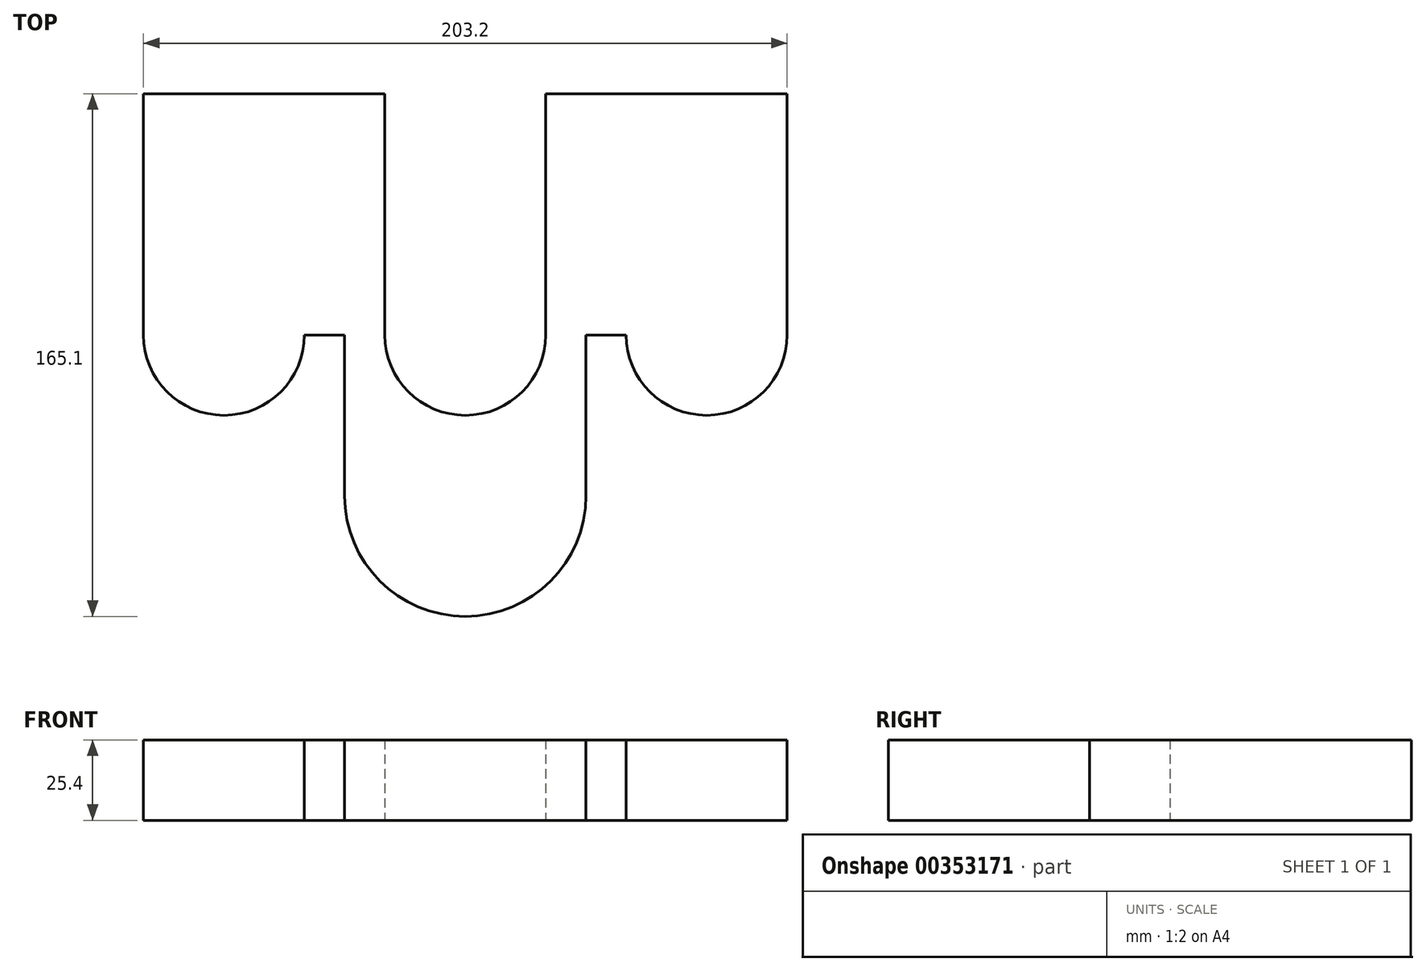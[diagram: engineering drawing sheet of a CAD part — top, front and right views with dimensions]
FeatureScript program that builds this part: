
annotation { "Feature Type Name" : "Feature", "Feature Type Description" : "" }
export const myFeature = defineFeature(function(context is Context, id is Id, definition is map)
    precondition{}
    {
        {
            var Q0;
            Q0=qCreatedBy(makeId("Top.planeOp"),FACE);
            var sketch = newSketch(context, id + "F0", { "sketchPlane" : qUnion([Q0])});
            skLineSegment(sketch, "E0", {"start": v(-50.8, 37.25) * mm, "end": v(25.4, 37.25) * mm});
            skLineSegment(sketch, "E1", {"start": v(25.4, 37.25) * mm, "end": v(25.4, -38.95) * mm});
            skLineSegment(sketch, "E2", {"start": v(-50.8, 37.25) * mm, "end": v(-50.8, -38.95) * mm});
            skArc(sketch, "E3", {"start": v(-50.8, -38.95) * mm, "mid": v(-25.4, -64.35) * mm, "end": v(0, -38.95) * mm});
            skLineSegment(sketch, "E4", {"start": v(-50.8, -38.95) * mm, "end": v(0, -38.95) * mm, "construction": true});
            skArc(sketch, "E5", {"start": v(25.4, -38.95) * mm, "mid": v(32.84, -56.91) * mm, "end": v(50.8, -64.35) * mm});
            skLineSegment(sketch, "E6", {"start": v(50.8, -38.95) * mm, "end": v(50.8, -85.52) * mm, "construction": true});
            skLineSegment(sketch, "E7", {"start": v(0, -38.95) * mm, "end": v(12.7, -38.95) * mm});
            skLineSegment(sketch, "E8", {"start": v(12.7, -38.95) * mm, "end": v(12.7, -89.75) * mm});
            skArc(sketch, "E9", {"start": v(12.7, -89.75) * mm, "mid": v(23.86, -116.7) * mm, "end": v(50.8, -127.85) * mm});
            skArc(sketch, "E10.MirrorCS", {"start": v(88.9, -89.75) * mm, "mid": v(77.74, -116.7) * mm, "end": v(50.8, -127.85) * mm});
            skLineSegment(sketch, "E11.MirrorCS", {"start": v(88.9, -38.95) * mm, "end": v(88.9, -89.75) * mm});
            skArc(sketch, "E12.MirrorCS", {"start": v(76.2, -38.95) * mm, "mid": v(68.76, -56.91) * mm, "end": v(50.8, -64.35) * mm});
            skLineSegment(sketch, "E13.MirrorCS", {"start": v(101.6, -38.95) * mm, "end": v(88.9, -38.95) * mm});
            skArc(sketch, "E14.MirrorCS", {"start": v(152.4, -38.95) * mm, "mid": v(127, -64.35) * mm, "end": v(101.6, -38.95) * mm});
            skLineSegment(sketch, "E15.MirrorCS", {"start": v(152.4, 37.25) * mm, "end": v(152.4, -38.95) * mm});
            skLineSegment(sketch, "E16.MirrorCS", {"start": v(76.2, 37.25) * mm, "end": v(76.2, -38.95) * mm});
            skLineSegment(sketch, "E17.MirrorCS", {"start": v(152.4, 37.25) * mm, "end": v(76.2, 37.25) * mm});
            skSolve(sketch);
        }
        {
            var Q0;
            Q0 = qSketchRegion(id + "F0", true);
            extrude(context, id + "F1", {"entities" : qUnion([Q0]), "depth" : 25.4 * mm});
        }
    });
